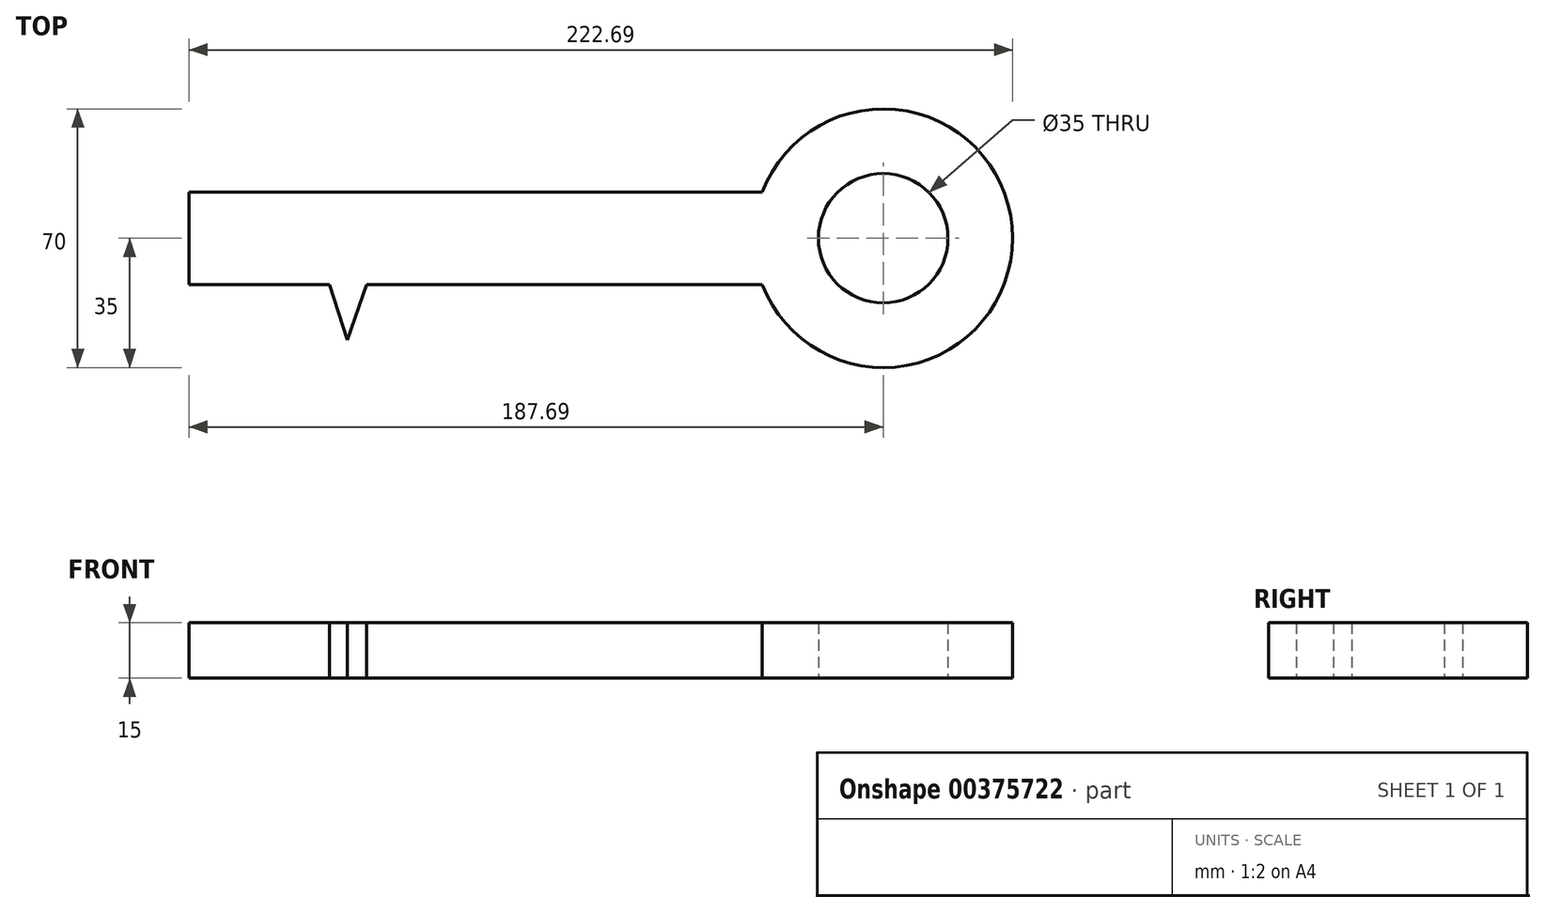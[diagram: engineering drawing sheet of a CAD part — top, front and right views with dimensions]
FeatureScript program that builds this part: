
annotation { "Feature Type Name" : "Feature", "Feature Type Description" : "" }
export const myFeature = defineFeature(function(context is Context, id is Id, definition is map)
    precondition{}
    {
        {
            var Q0;
            Q0=qCreatedBy(makeId("Top.planeOp"),FACE);
            var sketch = newSketch(context, id + "F0", { "sketchPlane" : qUnion([Q0])});
            skLineSegment(sketch, "E0.bottom", {"start": v(-160.18, 14.95) * mm, "end": v(-5.18, 14.95) * mm});
            skLineSegment(sketch, "E0.top", {"start": v(-160.18, -10.05) * mm, "end": v(-5.18, -10.05) * mm});
            skLineSegment(sketch, "E0.left", {"start": v(-160.18, 14.95) * mm, "end": v(-160.18, -10.05) * mm});
            skLineSegment(sketch, "E0.right", {"start": v(-5.18, 14.95) * mm, "end": v(-5.18, -10.05) * mm});
            skArc(sketch, "E1", {"start": v(-5.18, -10.05) * mm, "mid": v(62.51, 2.45) * mm, "end": v(-5.18, 14.95) * mm});
            skCircle(sketch, "E2", {"center": v(27.51, 2.45) * mm, "radius": 17.5 * mm});
            skLineSegment(sketch, "E3.bottom", {"start": v(-160.18, -10.05) * mm, "end": v(-150.18, -10.05) * mm});
            skLineSegment(sketch, "E3.top", {"start": v(-160.18, -40.05) * mm, "end": v(-150.18, -40.05) * mm});
            skLineSegment(sketch, "E3.left", {"start": v(-160.18, -10.05) * mm, "end": v(-160.18, -40.05) * mm});
            skLineSegment(sketch, "E3.right", {"start": v(-150.18, -10.05) * mm, "end": v(-150.18, -40.05) * mm});
            skLineSegment(sketch, "E4.bottom", {"start": v(-140.18, -10.05) * mm, "end": v(-132.18, -10.05) * mm});
            skLineSegment(sketch, "E4.top", {"start": v(-140.18, -25.05) * mm, "end": v(-132.18, -25.05) * mm});
            skLineSegment(sketch, "E4.left", {"start": v(-140.18, -10.05) * mm, "end": v(-140.18, -25.05) * mm});
            skLineSegment(sketch, "E4.right", {"start": v(-132.18, -10.05) * mm, "end": v(-132.18, -25.05) * mm});
            skLineSegment(sketch, "E5", {"start": v(-122.18, -10.05) * mm, "end": v(-117.3, -25.05) * mm});
            skLineSegment(sketch, "E6", {"start": v(-117.3, -25.05) * mm, "end": v(-112.18, -10.05) * mm});
            skSolve(sketch);
        }
        {
            var Q0;
            Q0=makeQuery(id+"F0.imprint","IMPRINT",FACE,{"disambiguationData":[TD([[makeQuery(id+"F0.imprint","IMPRINT",EDGE,{"derivedFrom":sQuery(id+"F0.wireOp",EDGE,"E0.bottom")}),-1.0]])]});
            var Q1;
            Q1=makeQuery(id+"F0.imprint","IMPRINT",FACE,{"disambiguationData":[TD([[makeQuery(id+"F0.imprint","IMPRINT",EDGE,{"derivedFrom":sQuery(id+"F0.wireOp",EDGE,"E3.bottom")}),-1.0]])]});
            var Q2;
            Q2=makeQuery(id+"F0.imprint","IMPRINT",FACE,{"disambiguationData":[TD([[makeQuery(id+"F0.imprint","IMPRINT",EDGE,{"derivedFrom":sQuery(id+"F0.wireOp",EDGE,"E4.bottom")}),-1.0]])]});
            var Q3;
            {var subQ0=sQuery(id+"F0.wireOp",EDGE,"E5");Q3=makeQuery(id+"F0.imprint","IMPRINT",FACE,{"disambiguationData":[TD([[makeQuery(id+"F0.imprint","IMPRINT",EDGE,{"derivedFrom":subQ0}),1.0]])]});}
            var Q4;
            Q4=makeQuery(id+"F0.imprint","IMPRINT",FACE,{"disambiguationData":[TD([[makeQuery(id+"F0.imprint","IMPRINT",EDGE,{"derivedFrom":sQuery(id+"F0.wireOp",EDGE,"E0.right")}),1.0]])]});
            extrude(context, id + "F1", {"entities" : qUnion([Q0, Q1, Q2, Q3, Q4]), "depth" : 15 * mm});
        }
    });
